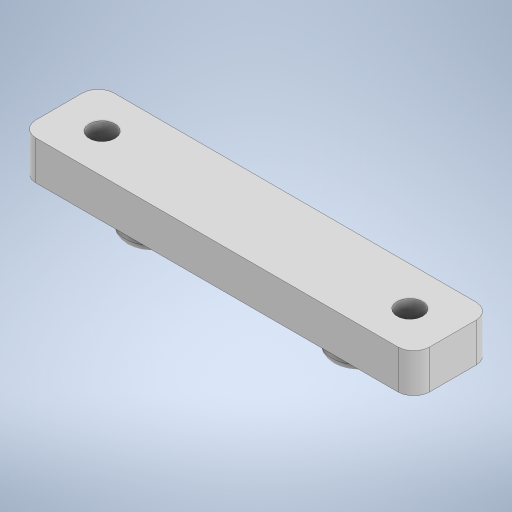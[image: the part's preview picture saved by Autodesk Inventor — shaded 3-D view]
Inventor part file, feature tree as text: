
AUTODESK INVENTOR PART (.ipt)
format: ipt  version: 2024 (Build 280153000, 153)  size: 256,512 bytes
history: native  units: mm
features: extrude x2, other x1, sketch x1, fillet x1
ambient origin geometry x8: Origin, YZ Plane, XZ Plane, XY Plane, X Axis, Y Axis, Z Axis, Center Point
bodies: Body1 (feature_tree)
feature tree (5):
  other  "Твердое тело1"
  sketch  "Эскиз1"
  extrude  "Выдавливание1"  Depth=7.0mm
  extrude  "Выдавливание2"  Depth=7.0mm
  fillet  "Сопряжение1"  Radius=19.5mm
